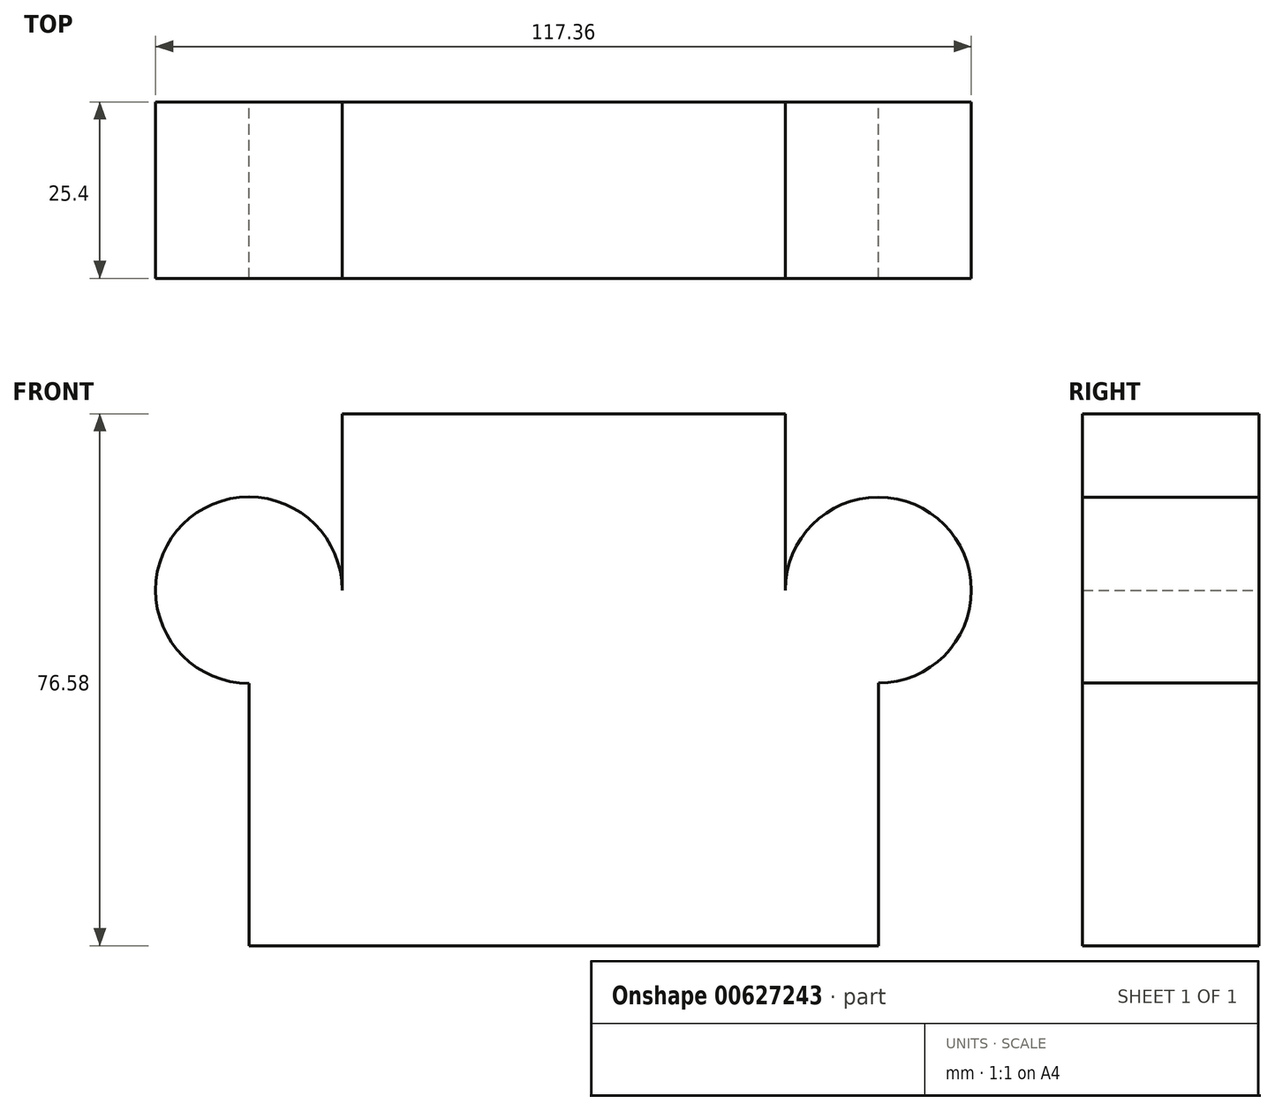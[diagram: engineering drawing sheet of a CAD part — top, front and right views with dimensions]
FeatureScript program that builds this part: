
annotation { "Feature Type Name" : "Feature", "Feature Type Description" : "" }
export const myFeature = defineFeature(function(context is Context, id is Id, definition is map)
    precondition{}
    {
        {
            var Q0;
            Q0=qCreatedBy(makeId("Front.planeOp"),FACE);
            var sketch = newSketch(context, id + "F0", { "sketchPlane" : qUnion([Q0])});
            skLineSegment(sketch, "E0.bottom", {"start": v(-122.6, 56.68) * mm, "end": v(-32.05, 56.68) * mm});
            skLineSegment(sketch, "E0.top", {"start": v(-122.6, 5.5) * mm, "end": v(-32.05, 5.5) * mm});
            skLineSegment(sketch, "E0.left", {"start": v(-122.6, 56.68) * mm, "end": v(-122.6, 5.5) * mm});
            skLineSegment(sketch, "E0.right", {"start": v(-32.05, 56.68) * mm, "end": v(-32.05, 5.5) * mm});
            skCircle(sketch, "E1", {"center": v(-122.6, 56.68) * mm, "radius": 13.42 * mm});
            skCircle(sketch, "E2", {"center": v(-32.05, 56.68) * mm, "radius": 13.38 * mm});
            skSolve(sketch);
        }
        {
            var Q0;
            Q0 = qSketchRegion(id + "F0", true);
            extrude(context, id + "F1", {"entities" : qUnion([Q0]), "depth" : 25.4 * mm, "offsetDistance" : 25.4 * mm});
        }
        {
            var Q0;
            Q0=makeQuery(id+"F1.opExtrude","SWEPT_FACE",FACE,{"disambiguationData":[OSD([sQuery(id+"F0.wireOp",EDGE,"E0.bottom")])]});
            extrude(context, id + "F2", {"entities" : qUnion([Q0]), "operationType" : NewBodyOperationType.ADD, "depth" : 25.4 * mm, "offsetDistance" : 25.4 * mm});
        }
        {
            var Q0;
            {var subQ0=sQuery(id+"F0.wireOp",EDGE,"E0.bottom");Q0=makeQuery(id+"F2.boolean.opBoolean","MERGE",FACE,{"derivedFrom":[makeQuery(id+"F1.opExtrude","CAP_FACE",FACE,{"disambiguationData":[OSD([subQ0,sQuery(id+"F0.wireOp",EDGE,"E0.top"),sQuery(id+"F0.wireOp",EDGE,"E0.left"),sQuery(id+"F0.wireOp",EDGE,"E0.right"),sQuery(id+"F0.wireOp",EDGE,"E1"),sQuery(id+"F0.wireOp",EDGE,"E2")])],"isStart":false}),makeQuery(id+"F2.opExtrude","SWEPT_FACE",FACE,{"disambiguationData":[OSD([subQ0]),TDD([makeQuery(id+"F1.opExtrude","CAP_EDGE",EDGE,{"disambiguationData":[OSD([subQ0])],"isStart":false})])]})]});}
            var sketch = newSketch(context, id + "F3", { "sketchPlane" : qUnion([Q0])});
            skCircle(sketch, "E3", {"center": v(-122.6, 56.68) * mm, "radius": 8.32 * mm});
            skCircle(sketch, "E4", {"center": v(-32.05, 56.68) * mm, "radius": 10 * mm});
            skSolve(sketch);
        }
        {
            var Q0;
            Q0=makeQuery(id+"F3.imprint","IMPRINT",FACE,{"disambiguationData":[TD([[makeQuery(id+"F3.imprint","IMPRINT",EDGE,{"derivedFrom":sQuery(id+"F3.wireOp",EDGE,"E4")}),1.0]])]});
            extrude(context, id + "F4", {"entities" : qUnion([Q0]), "operationType" : NewBodyOperationType.ADD, "oppositeDirection" : true, "depth" : 25.4 * mm, "offsetDistance" : 25.4 * mm});
        }
    });
